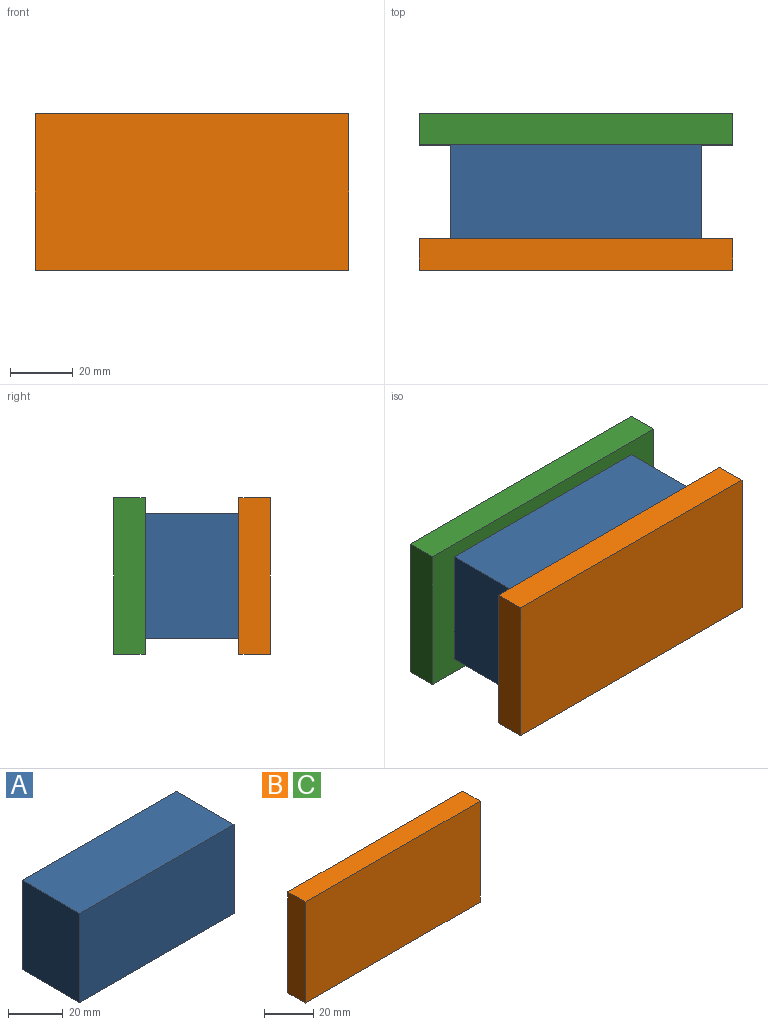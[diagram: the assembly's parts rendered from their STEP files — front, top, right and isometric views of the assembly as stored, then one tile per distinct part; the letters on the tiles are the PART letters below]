
ASSEMBLY  parts=3 mates=2
PART A: 6 faces, bbox 80x30x40 mm
  f0: plane 80x30mm, normal (0,0,1), area 2400mm2, adj f1,f3,f4,f5
  f1: plane 40x30mm, normal (-1,0,0), area 1200mm2, adj f0,f2,f4,f5
  f2: plane 80x30mm, normal (0,0,-1), area 2400mm2, adj f1,f3,f4,f5
  f3: plane 40x30mm, normal (1,0,0), area 1200mm2, adj f0,f2,f4,f5
  f4: plane 80x40mm, normal (0,-1,0), area 3200mm2, adj f0,f1,f2,f3
  f5: plane 80x40mm, normal (0,1,0), area 3200mm2, adj f0,f1,f2,f3
PART B: 6 faces, bbox 100x10x50 mm
  f0: plane 100x10mm, normal (0,0,1), area 1000mm2, adj f1,f3,f4,f5
  f1: plane 50x10mm, normal (-1,0,0), area 500mm2, adj f0,f2,f4,f5
  f2: plane 100x10mm, normal (0,0,-1), area 1000mm2, adj f1,f3,f4,f5
  f3: plane 50x10mm, normal (1,0,0), area 500mm2, adj f0,f2,f4,f5
  f4: plane 100x50mm, normal (0,-1,0), area 5000mm2, adj f0,f1,f2,f3
  f5: plane 100x50mm, normal (0,1,0), area 5000mm2, adj f0,f1,f2,f3
PART C: same geometry as B
PLACE A t=(-28.23,-14.59,-15.63)mm
PLACE B t=(-38.23,-44.59,-10.63)mm
PLACE C t=(-38.23,-4.59,-10.63)mm
MATE fastened B.f5 <-> A.f4  axis (0,1,0) through (11.77,-44.59,-35.63)mm
MATE fastened C.f4 <-> A.f5  axis (0,-1,0) through (11.77,-14.59,-35.63)mm
